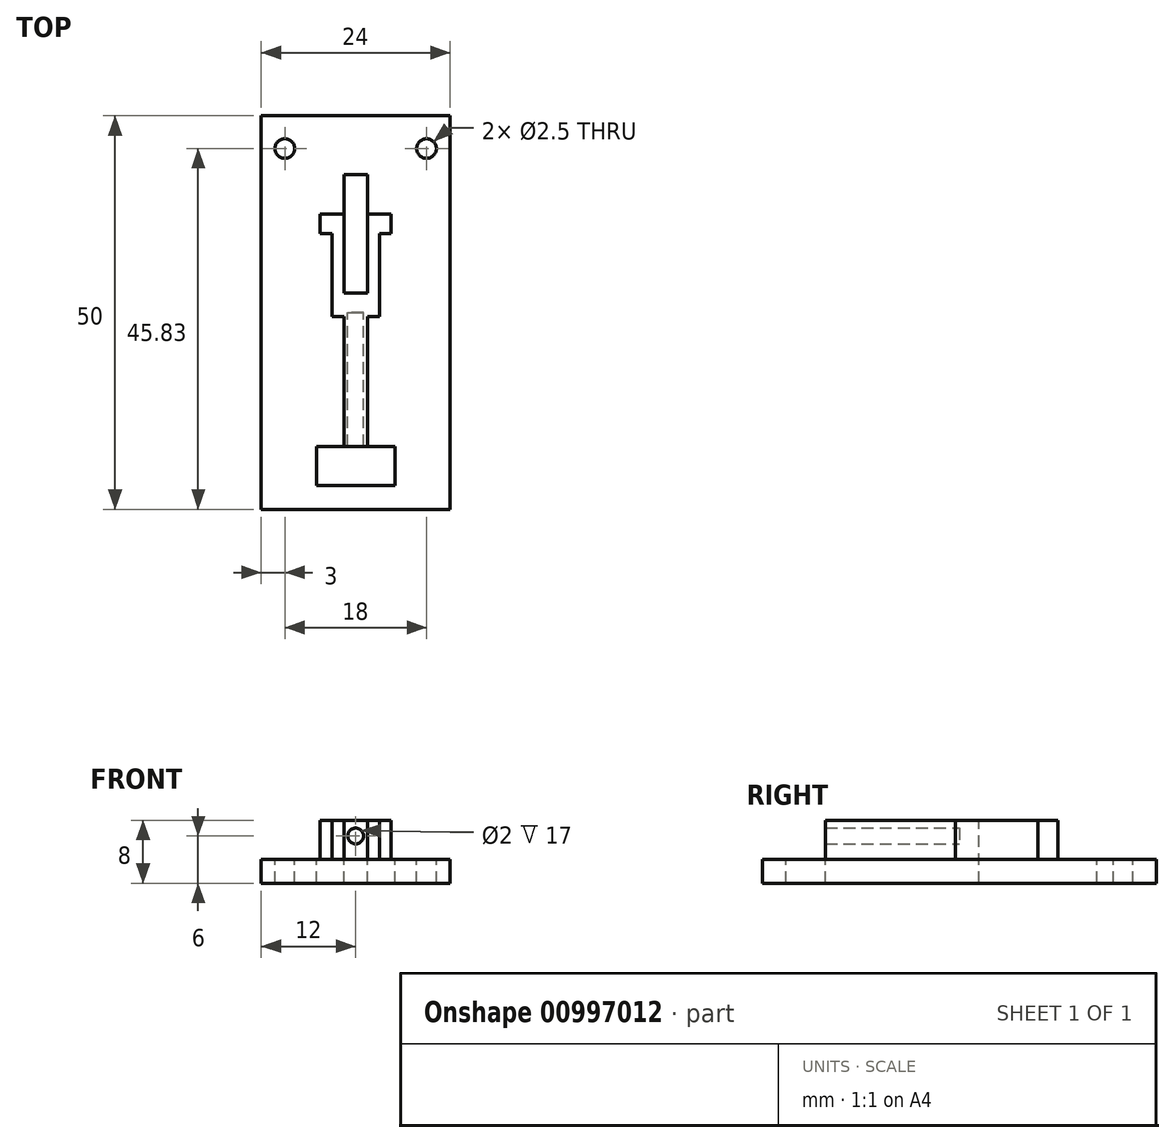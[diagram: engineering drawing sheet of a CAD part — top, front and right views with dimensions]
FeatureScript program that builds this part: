
annotation { "Feature Type Name" : "Feature", "Feature Type Description" : "" }
export const myFeature = defineFeature(function(context is Context, id is Id, definition is map)
    precondition{}
    {
        {
            var Q0;
            Q0=qCreatedBy(makeId("Top.planeOp"),FACE);
            var sketch = newSketch(context, id + "F0", { "sketchPlane" : qUnion([Q0])});
            skLineSegment(sketch, "E0.bottom", {"start": v(12, 25) * mm, "end": v(-12, 25) * mm});
            skLineSegment(sketch, "E0.top", {"start": v(12, -25) * mm, "end": v(-12, -25) * mm});
            skLineSegment(sketch, "E0.left", {"start": v(12, 25) * mm, "end": v(12, -25) * mm});
            skLineSegment(sketch, "E0.right", {"start": v(-12, 25) * mm, "end": v(-12, -25) * mm});
            skPoint(sketch, "E0.middle", {"position": v(0, 0) * mm});
            skPoint(sketch, "E1", {"position": v(-9, 20.83) * mm});
            skPoint(sketch, "E2", {"position": v(9, 20.83) * mm});
            skCircle(sketch, "E3", {"center": v(-9, 20.83) * mm, "radius": 1.25 * mm});
            skCircle(sketch, "E4", {"center": v(9, 20.83) * mm, "radius": 1.25 * mm});
            skLineSegment(sketch, "E5.bottom", {"start": v(-1.5, 17.5) * mm, "end": v(1.5, 17.5) * mm});
            skLineSegment(sketch, "E5.top", {"start": v(-1.5, 2.5) * mm, "end": v(1.5, 2.5) * mm});
            skLineSegment(sketch, "E5.left", {"start": v(-1.5, 17.5) * mm, "end": v(-1.5, 2.5) * mm});
            skLineSegment(sketch, "E5.right", {"start": v(1.5, 17.5) * mm, "end": v(1.5, 2.5) * mm});
            skPoint(sketch, "E5.middle", {"position": v(0, 10) * mm});
            skPoint(sketch, "E6", {"position": v(1.5, 12.5) * mm});
            skPoint(sketch, "E7", {"position": v(-1.5, 12.5) * mm});
            skLineSegment(sketch, "E8.bottom", {"start": v(-5, -17) * mm, "end": v(5, -17) * mm});
            skLineSegment(sketch, "E9", {"start": v(-5, -17) * mm, "end": v(-5, -22) * mm});
            skLineSegment(sketch, "E10", {"start": v(-5, -22) * mm, "end": v(5, -22) * mm});
            skLineSegment(sketch, "E11", {"start": v(5, -22) * mm, "end": v(5, -17) * mm});
            skPoint(sketch, "E12", {"position": v(-1.5, -17) * mm});
            skPoint(sketch, "E13", {"position": v(1.5, -17) * mm});
            skLineSegment(sketch, "E14", {"start": v(-3, -0.5) * mm, "end": v(-3, 10) * mm});
            skPoint(sketch, "E15", {"position": v(-1.5, -0.5) * mm});
            skLineSegment(sketch, "E16", {"start": v(-3, -0.5) * mm, "end": v(-1.5, -0.5) * mm});
            skLineSegment(sketch, "E17", {"start": v(-1.5, -17) * mm, "end": v(-1.5, -0.5) * mm});
            skLineSegment(sketch, "E18", {"start": v(-3, 10) * mm, "end": v(-1.5, 10) * mm});
            skLineSegment(sketch, "E19.MirrorCS", {"start": v(3, -0.5) * mm, "end": v(3, 10) * mm});
            skLineSegment(sketch, "E20.MirrorCS", {"start": v(3, 10) * mm, "end": v(1.5, 10) * mm});
            skLineSegment(sketch, "E21.MirrorCS", {"start": v(3, -0.5) * mm, "end": v(1.5, -0.5) * mm});
            skLineSegment(sketch, "E22.MirrorCS", {"start": v(1.5, -17) * mm, "end": v(1.5, -0.5) * mm});
            skSolve(sketch);
        }
        {
            var Q0;
            Q0=qCreatedBy(makeId("Right.planeOp"),FACE);
            var sketch = newSketch(context, id + "F1", { "sketchPlane" : qUnion([Q0])});
            skLineSegment(sketch, "E23", {"start": v(12.5, 0) * mm, "end": v(12.5, 5) * mm});
            skLineSegment(sketch, "E24", {"start": v(12.5, 5) * mm, "end": v(10, 5) * mm});
            skLineSegment(sketch, "E25", {"start": v(10, 5) * mm, "end": v(10, 0) * mm});
            skLineSegment(sketch, "E26", {"start": v(10, 0) * mm, "end": v(12.5, 0) * mm});
            skPoint(sketch, "E27", {"position": v(12.5, 3) * mm});
            skSolve(sketch);
        }
        {
            var Q0;
            Q0=qCreatedBy(makeId("Right.planeOp"),FACE);
            cPlane(context, id + "F2", {"entities" : qUnion([Q0]), "cplaneType" : CPlaneType.OFFSET, "offset" : 1.5 * mm, "oppositeDirection" : true, "width" : 152.4 * mm, "height" : 152.4 * mm});
        }
        {
            var Q0;
            Q0=qCreatedBy(makeId("Right.planeOp"),FACE);
            cPlane(context, id + "F3", {"entities" : qUnion([Q0]), "cplaneType" : CPlaneType.OFFSET, "offset" : 1.5 * mm, "width" : 152.4 * mm, "height" : 152.4 * mm});
        }
        {
            var Q0;
            Q0=makeQuery(id+"F1.imprint","IMPRINT",FACE,{"disambiguationData":[TD([[makeQuery(id+"F1.imprint","IMPRINT",EDGE,{"derivedFrom":sQuery(id+"F1.wireOp",EDGE,"E23")}),1.0]])]});
            extrude(context, id + "F4", {"entities" : qUnion([Q0]), "depth" : 4.5 * mm, "offsetDistance" : 25.4 * mm, "hasSecondDirection" : true, "secondDirectionOppositeDirection" : false, "secondDirectionDepth" : 1.5 * mm});
        }
        {
            var Q0;
            Q0=makeQuery(id+"F0.imprint","IMPRINT",FACE,{"disambiguationData":[TD([[makeQuery(id+"F0.imprint","IMPRINT",EDGE,{"derivedFrom":sQuery(id+"F0.wireOp",EDGE,"E0.bottom")}),1.0]])]});
            var Q1;
            {var subQ0=sQuery(id+"F0.wireOp",EDGE,"E5.top");Q1=makeQuery(id+"F0.imprint","IMPRINT",FACE,{"disambiguationData":[TD([[makeQuery(id+"F0.imprint","IMPRINT",EDGE,{"derivedFrom":subQ0}),-1.0]])]});}
            var Q2;
            Q2=makeQuery(id+"F0.imprint","IMPRINT",FACE,{"disambiguationData":[TD([[makeQuery(id+"F0.imprint","IMPRINT",EDGE,{"derivedFrom":sQuery(id+"F0.wireOp",EDGE,"E8.top")}),1.0]])]});
            extrude(context, id + "F5", {"entities" : qUnion([Q0, Q1, Q2]), "operationType" : NewBodyOperationType.ADD, "oppositeDirection" : true, "depth" : 3 * mm, "offsetDistance" : 25.4 * mm});
        }
        {
            var Q0;
            Q0=makeQuery(id+"F1.imprint","IMPRINT",FACE,{"disambiguationData":[TD([[makeQuery(id+"F1.imprint","IMPRINT",EDGE,{"derivedFrom":sQuery(id+"F1.wireOp",EDGE,"E23")}),1.0]])]});
            extrude(context, id + "F6", {"entities" : qUnion([Q0]), "operationType" : NewBodyOperationType.ADD, "oppositeDirection" : true, "depth" : 4.5 * mm, "offsetDistance" : 25.4 * mm, "hasSecondDirection" : true, "secondDirectionOppositeDirection" : true, "secondDirectionDepth" : 1.5 * mm});
        }
        {
            var Q0;
            {var subQ2=sQuery(id+"F0.wireOp",EDGE,"E5.top");Q0=makeQuery(id+"F0.imprint","IMPRINT",FACE,{"disambiguationData":[TD([[makeQuery(id+"F0.imprint","IMPRINT",EDGE,{"derivedFrom":subQ2}),-1.0]])]});}
            extrude(context, id + "F7", {"entities" : qUnion([Q0]), "operationType" : NewBodyOperationType.ADD, "depth" : 5 * mm, "offsetDistance" : 25.4 * mm});
        }
        {
            var Q0;
            Q0=qCreatedBy(makeId("Front.planeOp"),FACE);
            var sketch = newSketch(context, id + "F8", { "sketchPlane" : qUnion([Q0])});
            skPoint(sketch, "E28", {"position": v(0, 3) * mm});
            skSolve(sketch);
        }
        {
            var Q0;
            Q0=sQuery(id+"F8.wireOp",VERTEX,"E28");
            var Q1;
            Q1=makeQuery(id+"F4.opExtrude","SWEPT_BODY",BODY,{"disambiguationData":[OSD([sQuery(id+"F1.wireOp",EDGE,"E23"),sQuery(id+"F1.wireOp",EDGE,"E24"),sQuery(id+"F1.wireOp",EDGE,"E25"),sQuery(id+"F1.wireOp",EDGE,"E26")])]});
            hole(context, id + "F9", {"style" : HoleStyle.SIMPLE, "endStyle" : HoleEndStyle.THROUGH, "oppositeDirection" : true, "holeDiameter" : 2 * mm, "majorDiameter" : 6.35 * mm, "isTappedThrough" : true, "tappedDepth" : 12.7 * mm, "tapClearance" : 3, "locations" : qUnion([Q0]), "scope" : qUnion([Q1])});
        }
    });
